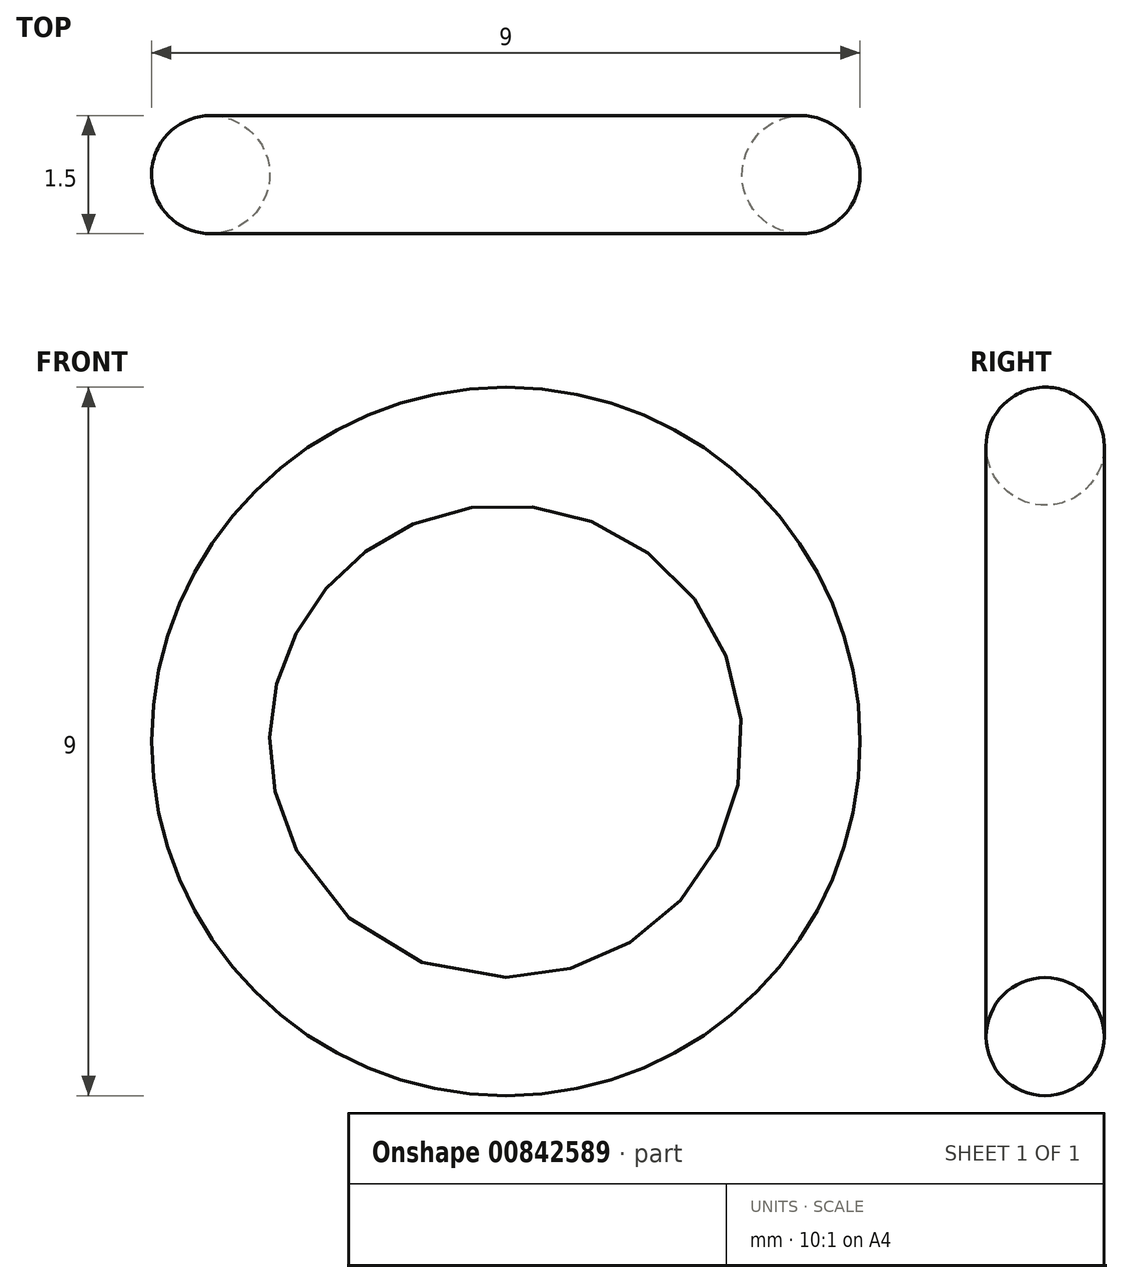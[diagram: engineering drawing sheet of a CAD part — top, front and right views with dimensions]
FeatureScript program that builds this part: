
annotation { "Feature Type Name" : "Feature", "Feature Type Description" : "" }
export const myFeature = defineFeature(function(context is Context, id is Id, definition is map)
    precondition{}
    {
        {
            var Q0;
            Q0=qCreatedBy(makeId("Right.planeOp"),FACE);
            var sketch = newSketch(context, id + "F0", { "sketchPlane" : qUnion([Q0])});
            skCircle(sketch, "E0", {"center": v(0, 3.75) * mm, "radius": 0.75 * mm});
            skLineSegment(sketch, "E1", {"start": v(-17.8, 0) * mm, "end": v(11.83, 0) * mm});
            skSolve(sketch);
        }
        {
            var Q0;
            Q0 = qSketchRegion(id + "F0", true);
            var Q1;
            Q1=sQuery(id+"F0.wireOp",EDGE,"E1");
            revolve(context, id + "F1", {"surfaceOperationType" : NewSurfaceOperationType.NEW, "entities" : qUnion([Q0]), "axis" : qUnion([Q1]), "revolveType" : RevolveType.FULL});
        }
    });
